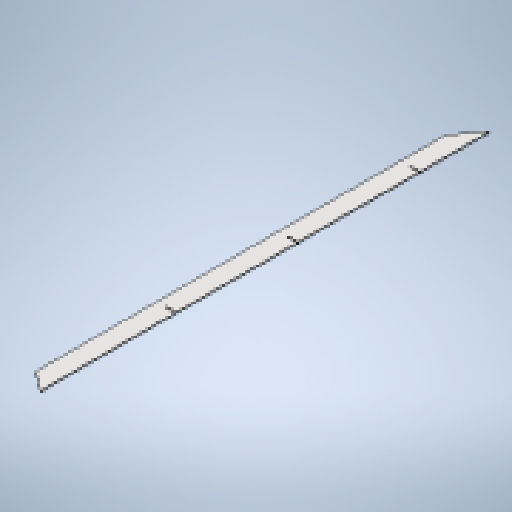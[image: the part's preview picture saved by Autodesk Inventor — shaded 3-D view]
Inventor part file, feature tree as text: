
AUTODESK INVENTOR PART (.ipt)
format: ipt  version: 2025 (Build 290162010, 162A)  size: 339,968 bytes
history: native  units: mm
features: other x5, sketch x3, chamfer x2, sheet_metal_op x1, extrude x1, pattern_linear x1
ambient origin geometry x8: Origin, YZ Plane, XZ Plane, XY Plane, X Axis, Y Axis, Z Axis, Center Point
bodies: Solid1 (feature_tree)
feature tree (13):
  sheet_metal_op  "Face1"
  other  "Corner Chamfer1"
  chamfer  "Corner Round1"
  chamfer  "Corner Round2"
  other  "Corner Chamfer3"
  extrude  "Extrusion1"  Depth=1190.0mm
  pattern_linear  "Rectangular Pattern1"  Spacing1=9.372418mm  [1 undecoded]
  other  "Mark1"
  sketch  "Sketch1"  dims[d0=50.0mm d1=1190.0mm]
  other  "Plate1"
  sketch  "Sketch3"  dims[d2=3.0mm]
  sketch  "Sketch4"  dims[d5=9.372418mm d6=9.372418mm d7=3.0mm d8=6.0mm d9=45.0deg d13=6.0mm d14=6.0mm d15=3.0mm d16=6.0mm d17=45.0deg d18=187.0mm d19=26.0mm d20=3.0mm d21=0.0mm d22=0.0mm d23=30.0mm d25=323.0mm]
  other  "Definition1"
note: 1 required parameter value undecoded (feature->parameter linkage not recoverable at this tier; creation-order binding heuristic only, values carry confidence <= 0.55)
